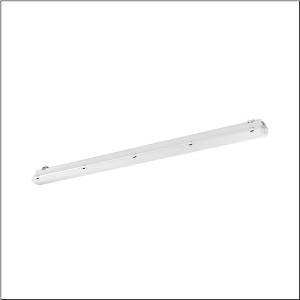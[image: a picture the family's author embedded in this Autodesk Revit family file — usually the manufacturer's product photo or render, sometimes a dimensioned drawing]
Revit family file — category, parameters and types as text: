
# Revit family: monsun_r__11xtreme_ho_51fe10dp480r_f689
name_source: partatom
category: Lighting Fixtures
units: mm (PartAtom-declared; Revit-internal decimal feet)

## family parameters
Cut with Voids When Loaded = No
Host = Face
Light Source = No
Part Type = Normal
Room Calculation Point = No
Round Connector Dimension = Use Diameter
Shared = No

## types (1)
- --- (1 x LED, 8000 lm, 44.3 W, 4000K)
    Apparent Load = 44 VA
    CIE Flux Codes = 47 76 93 94 100
    Color Rendering = 80
    Color Temperature = 4000K
    Default Elevation = 1800 mm
    Description = Monsun® 11Xtreme HO, damp-proof luminaire, chain hanger, primary optical cover: enclosure, of PMMA, light emission: direct distribution, primary light characteristic: symmetric, installation type: suspended mounting, surface-mounted, horizontal mounting, vertical mounting, LED, rated luminous flux: 8.000lm, luminous efficacy: 181lm/W, light colour: 840, colour temperature: 4000K, control gear: ECG DALI, with terminal, 5-pole, max. 2.5mm², mains connection: 220..240V, AC, 50/60Hz, rated input power: 44W, luminaire housing, of glass-fibre reinforced polyester, uncoated, bright grey, incl. chain hanger, length: 1.590mm, width: 90mm, height: 88mm, clip for enclosure, of stainless steel (V2A), ceiling mounting element, of stainless steel (V2A), chain hanger, of stainless steel (V2A), protection rating (complete): IP66, insulation class (complete): insulation class I (protective earthing), certification: CE, ENEC, VDE, UKCA, protection symbol: D, impact resistance: IK04, permissible operating ambient temperature: -35..+55°C, standard: EN 60598-2-1, EN 50419, corresponds to IFS (International Featured Standards) requirements for safety and quality in the food industry, for indoor or canopied outdoor use, no direct snow, no direct sun, no direct rain, contact your sales advisor before using the luminaires in applications with unclear chemical exposure, large temperature fluctuations or condensation-forming humidity, LABS conformity tested according to VDMA 24364:2018-05, packaging unit: 1 piece
    Height = 88 mm
    Lamp = 1 x LED
    Lamp Light Flux = 8000 lm
    Lamp Power = 44.3 W
    Lamp count = 1
    Length = 1590 mm
    Luminous efficacy = 181 lm/W
    Manufacturer = Siteco
    ModVariant = No
    Model = 51FE10DP480R
    Mounting Place = Ceiling
    Mounting Type = Surface mounted
    Number of Poles = 1
    OnlyDefault = Yes
    Power Factor = 1
    Product Name = Monsun® 11Xtreme HO
    Product group = damp-proof luminaire
    ProductGroupID = 300
    Protection Class = Protection class I
    Protection Degree = IP 66
    RLX_Detail_Level = 1
    RLX_Emergency_Light_Flux = 0 lm
    RLX_Emergency_Type = 0
    RLX_Emergency_Type_DB = No
    RlxData = <blob elided: 87293 chars, md5=28e0363c>
    Socket = socket
    Standby Power = 0 W
    System Light Flux = 8000 lm
    System Power = 44 W
    Type Comments = factory setting: luminous flux: 100 % | dim-lin: 254 | 253 mA
    Type Image = l_1006851.jpg
    URL = http://relux.com
    VarID = @adj_133169
    Voltage = 0 V
    Weight = 0.00 kg
    Width = 90 mm

## geometry (parser evidence)
native form markers: Blend x4, Sweep x13
no freeform markers — native parametric forms only
